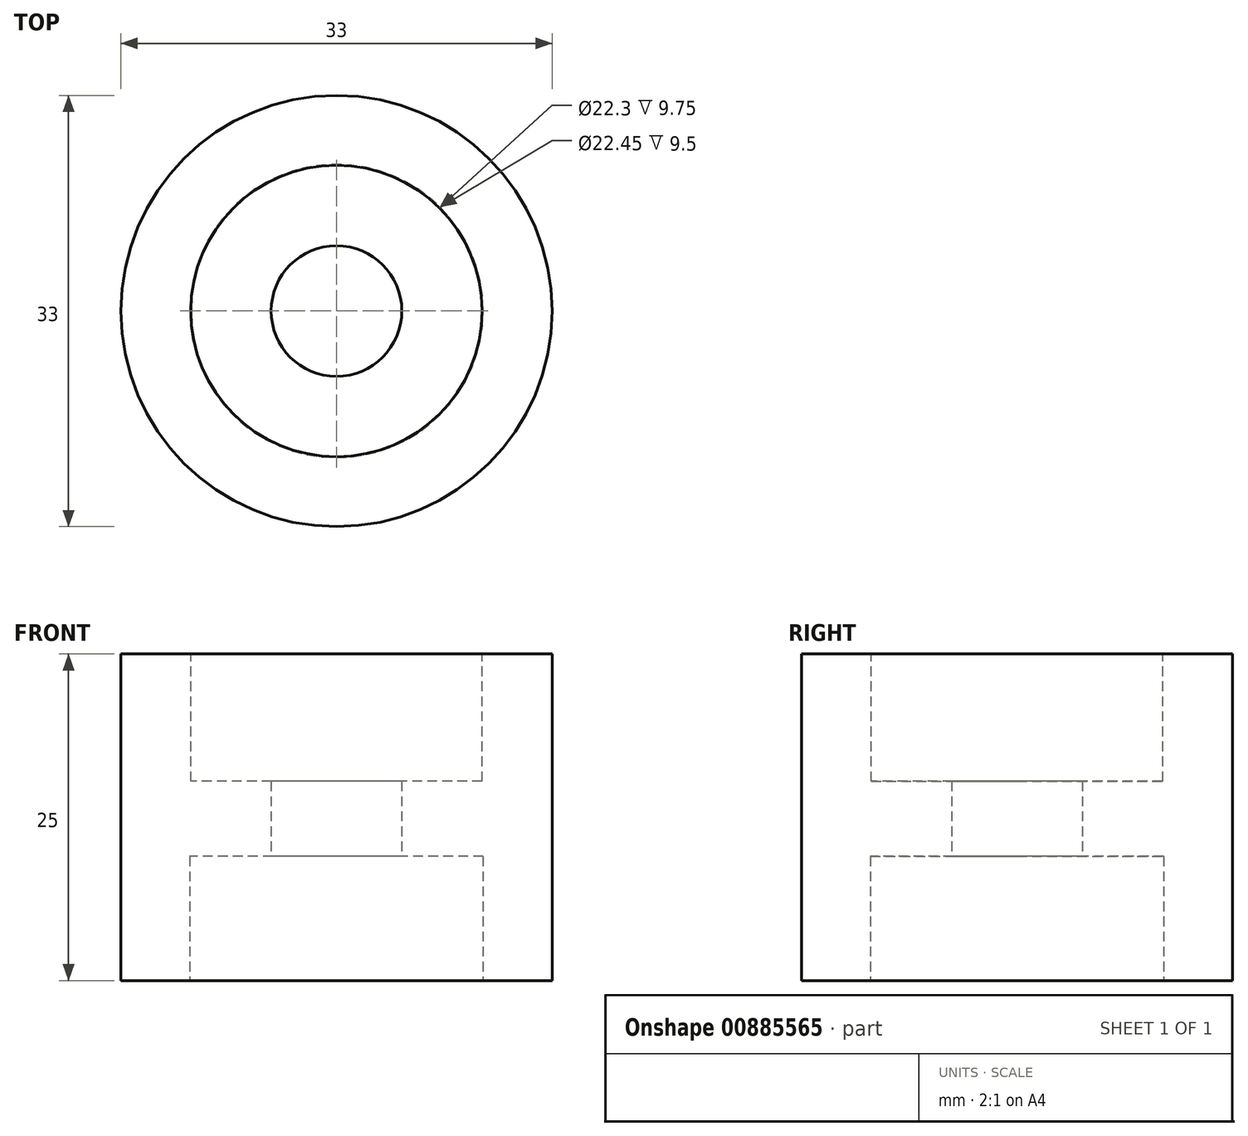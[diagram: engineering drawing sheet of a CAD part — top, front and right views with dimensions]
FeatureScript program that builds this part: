
annotation { "Feature Type Name" : "Feature", "Feature Type Description" : "" }
export const myFeature = defineFeature(function(context is Context, id is Id, definition is map)
    precondition{}
    {
        {
            var Q0;
            Q0=qCreatedBy(makeId("Top.planeOp"),FACE);
            var sketch = newSketch(context, id + "F0", { "sketchPlane" : qUnion([Q0])});
            skCircle(sketch, "E0", {"center": v(0, 0) * mm, "radius": 5 * mm});
            skCircle(sketch, "E1", {"center": v(0, 0) * mm, "radius": 16.5 * mm});
            skSolve(sketch);
        }
        {
            var Q0;
            Q0 = qSketchRegion(id + "F0", true);
            extrude(context, id + "F1", {"entities" : qUnion([Q0]), "depth" : 25 * mm, "offsetDistance" : 25 * mm});
        }
        {
            var Q0;
            Q0=makeQuery(id+"F1.opExtrude","CAP_FACE",FACE,{"disambiguationData":[OSD([sQuery(id+"F0.wireOp",EDGE,"E0"),sQuery(id+"F0.wireOp",EDGE,"E1")])],"isStart":false});
            var sketch = newSketch(context, id + "F2", { "sketchPlane" : qUnion([Q0])});
            skCircle(sketch, "E2", {"center": v(0, 0) * mm, "radius": 11.15 * mm});
            skSolve(sketch);
        }
        {
            var Q0;
            Q0 = qSketchRegion(id + "F2", true);
            extrude(context, id + "F3", {"entities" : qUnion([Q0]), "operationType" : NewBodyOperationType.REMOVE, "oppositeDirection" : true, "depth" : 9.75 * mm, "offsetDistance" : 25 * mm});
        }
        {
            var Q0;
            Q0=qCreatedBy(makeId("Top.planeOp"),FACE);
            var sketch = newSketch(context, id + "F4", { "sketchPlane" : qUnion([Q0])});
            skCircle(sketch, "E3", {"center": v(0, 0) * mm, "radius": 11.23 * mm});
            skSolve(sketch);
        }
        {
            var Q0;
            Q0 = qSketchRegion(id + "F4", true);
            extrude(context, id + "F5", {"entities" : qUnion([Q0]), "operationType" : NewBodyOperationType.REMOVE, "depth" : 9.5 * mm, "offsetDistance" : 25 * mm});
        }
    });
